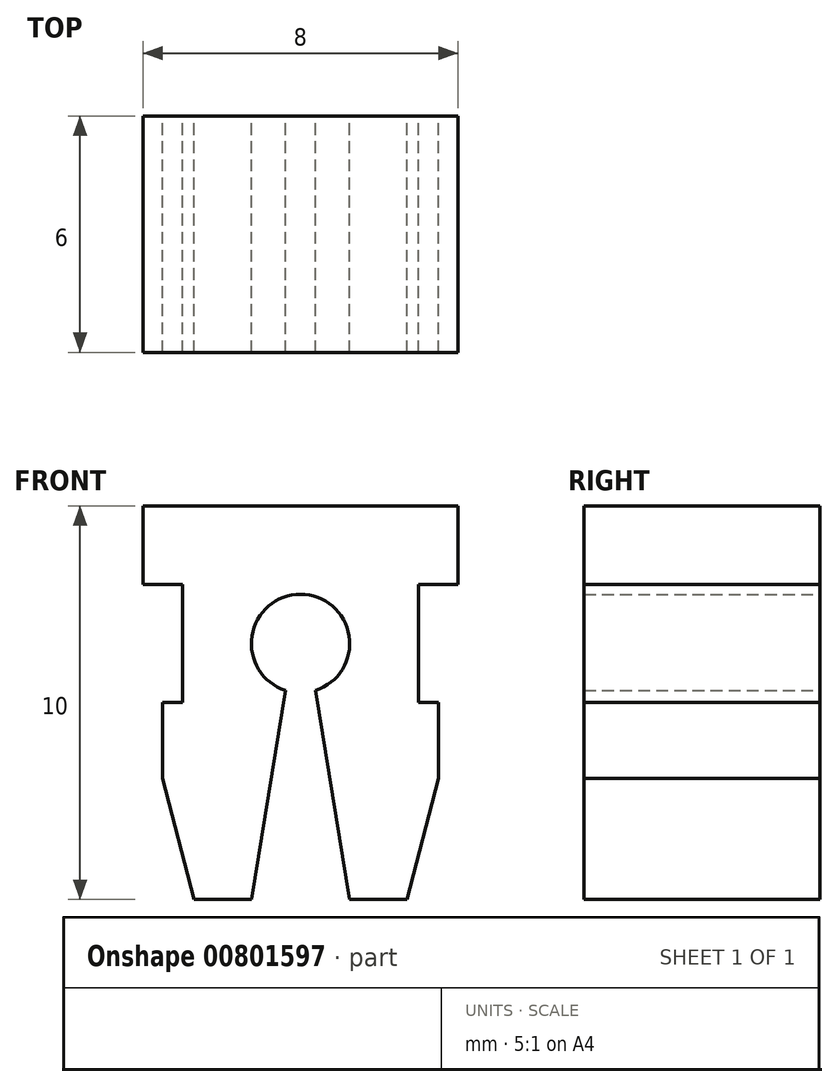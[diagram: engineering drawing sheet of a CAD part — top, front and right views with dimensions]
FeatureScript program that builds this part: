
annotation { "Feature Type Name" : "Feature", "Feature Type Description" : "" }
export const myFeature = defineFeature(function(context is Context, id is Id, definition is map)
    precondition{}
    {
        {
            var Q0;
            Q0=qCreatedBy(makeId("Front.planeOp"),FACE);
            var sketch = newSketch(context, id + "F0", { "sketchPlane" : qUnion([Q0])});
            skLineSegment(sketch, "E0.bottom", {"start": v(-4, 3.5) * mm, "end": v(4, 3.5) * mm});
            skLineSegment(sketch, "E0.top", {"start": v(-4, -6.5) * mm, "end": v(4, -6.5) * mm});
            skLineSegment(sketch, "E0.left", {"start": v(-4, 3.5) * mm, "end": v(-4, -6.5) * mm});
            skLineSegment(sketch, "E0.right", {"start": v(4, 3.5) * mm, "end": v(4, -6.5) * mm});
            skLineSegment(sketch, "E1.bottom", {"start": v(-4, 1.5) * mm, "end": v(-3, 1.5) * mm});
            skLineSegment(sketch, "E1.top", {"start": v(-4, -1.5) * mm, "end": v(-3, -1.5) * mm});
            skLineSegment(sketch, "E1.left", {"start": v(-4, 1.5) * mm, "end": v(-4, -1.5) * mm});
            skLineSegment(sketch, "E1.right", {"start": v(-3, 1.5) * mm, "end": v(-3, -1.5) * mm});
            skLineSegment(sketch, "E2.bottom", {"start": v(4, -1.5) * mm, "end": v(3, -1.5) * mm});
            skLineSegment(sketch, "E2.top", {"start": v(4, 1.5) * mm, "end": v(3, 1.5) * mm});
            skLineSegment(sketch, "E2.left", {"start": v(4, -1.5) * mm, "end": v(4, 1.5) * mm});
            skLineSegment(sketch, "E2.right", {"start": v(3, -1.5) * mm, "end": v(3, 1.5) * mm});
            skCircle(sketch, "E3", {"center": v(0, 0) * mm, "radius": 1.25 * mm});
            skLineSegment(sketch, "E4", {"start": v(-0.38, -1.2) * mm, "end": v(-1.25, -6.5) * mm});
            skLineSegment(sketch, "E5", {"start": v(0.38, -1.2) * mm, "end": v(1.25, -6.5) * mm});
            skLineSegment(sketch, "E6", {"start": v(-3.5, -1.5) * mm, "end": v(-3.5, -6.5) * mm});
            skLineSegment(sketch, "E7", {"start": v(3.5, -1.5) * mm, "end": v(3.5, -6.5) * mm});
            skLineSegment(sketch, "E8", {"start": v(-4, -1.5) * mm, "end": v(-2.7, -6.5) * mm});
            skLineSegment(sketch, "E9", {"start": v(4, -1.5) * mm, "end": v(2.7, -6.5) * mm});
            skLineSegment(sketch, "E10", {"start": v(-4.62, 0) * mm, "end": v(4.7, 0) * mm, "construction": true});
            skCircle(sketch, "E11", {"center": v(0, 0) * mm, "radius": 1.5 * mm, "construction": true});
            skSolve(sketch);
        }
        {
            var Q0;
            {var subQ7=sQuery(id+"F0.wireOp",EDGE,"E0.bottom");Q0=makeQuery(id+"F0.imprint","IMPRINT",FACE,{"disambiguationData":[TD([[makeQuery(id+"F0.imprint","IMPRINT",EDGE,{"derivedFrom":subQ7}),-1.0]])]});}
            extrude(context, id + "F1", {"entities" : qUnion([Q0]), "depth" : 6 * mm, "offsetDistance" : 25 * mm});
        }
    });
